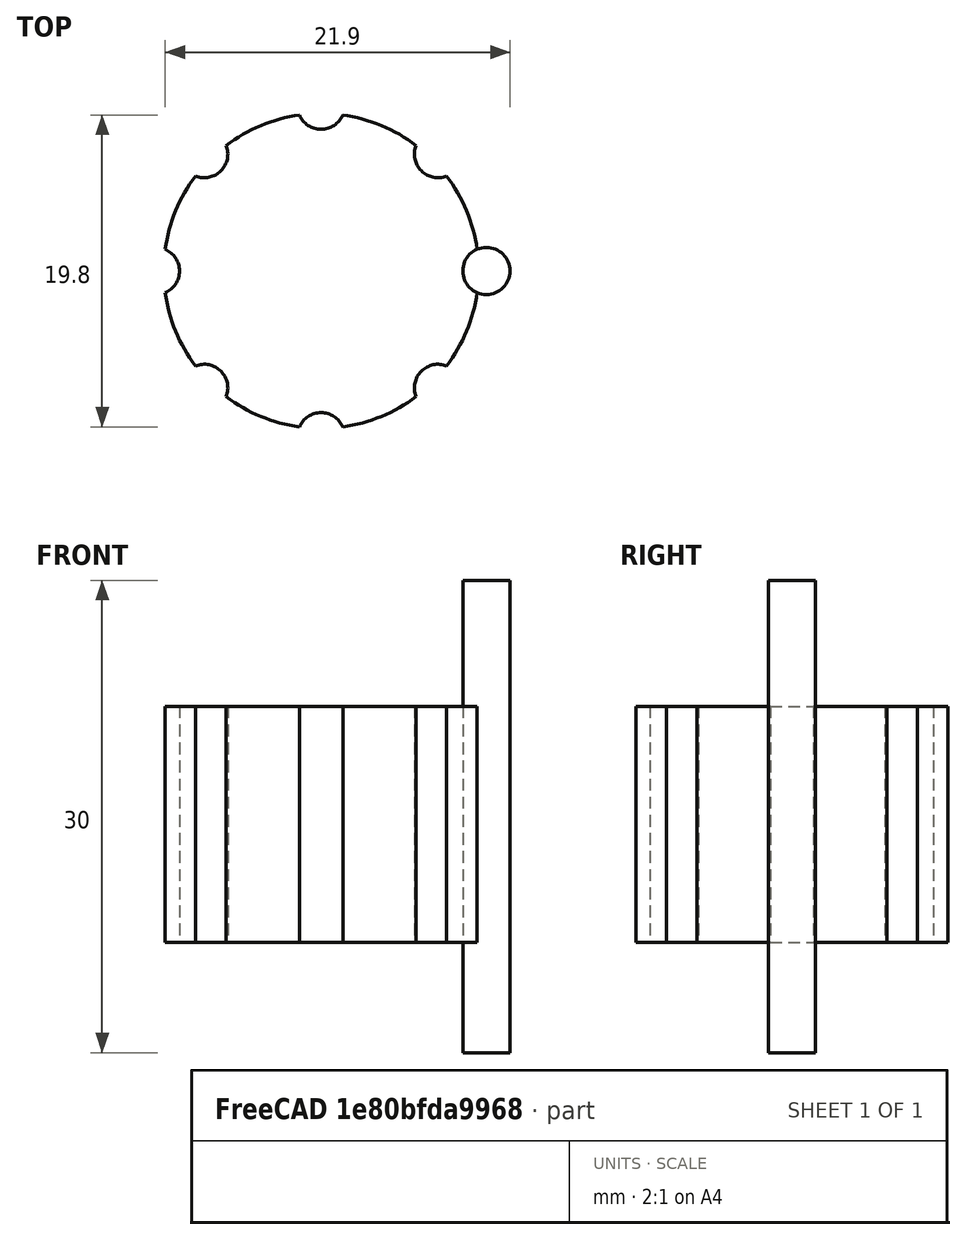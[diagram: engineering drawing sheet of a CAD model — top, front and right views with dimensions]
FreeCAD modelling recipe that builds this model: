
FCSTD DOCUMENT  (FreeCAD 0.21R33694 (Git))
Label: OJT1_T011R02
License: All rights reserved
LicenseURL: https://en.wikipedia.org/wiki/All_rights_reserved
objects: Part::Cylinder×2, Part::FeaturePython×1, Part::Cut×1
note: 3 computed .brp shape members not serialized (recipe doc carries the construction recipe); baked Part::Feature solids carry a one-line shape summary decoded from their .brp

FEATURE [Part::Cylinder] Cylinder  label="bASE"
  Angle = 360
  AttacherType = Attacher::AttachEngine3D
  FirstAngle = 0
  Height = 15
  Radius = 10
  SecondAngle = 0
FEATURE [Part::Cylinder] Cylinder001  label="Cilindre"
  Angle = 360
  AttacherType = Attacher::AttachEngine3D
  FirstAngle = 0
  Height = 30
  Placement = pos=(10.5,0,-7) rot=(0,0,1;0rad)
  Radius = 1.5
  SecondAngle = 0
  expr: .Placement.Base.x = 10.5 mm
FEATURE [Part::FeaturePython] Array  # Draft array (typed FeaturePython)
  AlwaysSyncPlacement = false
  Angle = 360
  ArrayType = 1
  Axis = (0,0,1)
  Base = -> Cylinder001
  Center = (0,0,0)
  Count = 8
  ExpandArray = false
  Fuse = false
  IntervalAxis = (0,0,0)
  IntervalX = (100,0,0)
  IntervalY = (0,100,0)
  IntervalZ = (0,0,100)
  NumberCircles = 3
  NumberPolar = 8
  NumberX = 2
  NumberY = 1
  NumberZ = 1
  PlacementList = 8 placements: [(10.5,0,-7),(7.42462,7.42462,-7),(0,10.5,-7),(-7.42462,7.42462,-7),(-10.5,1.28588e-15,-7),(-7.42462,-7.42462,-7),(-2.33147e-15,-10.5,-7),(7.42462,-7.42462,-7)]
  RadialDistance = 50
  ScaleList = (8) [(1,1,1),(1,1,1),(1,1,1),(1,1,1),(1,1,1),(1,1,1),(1,1,1),(1,1,1)]
  Symmetry = 1
  TangentialDistance = 25
FEATURE [Part::Cut] Cut
  Base = -> Cylinder
  Tool = -> Array
